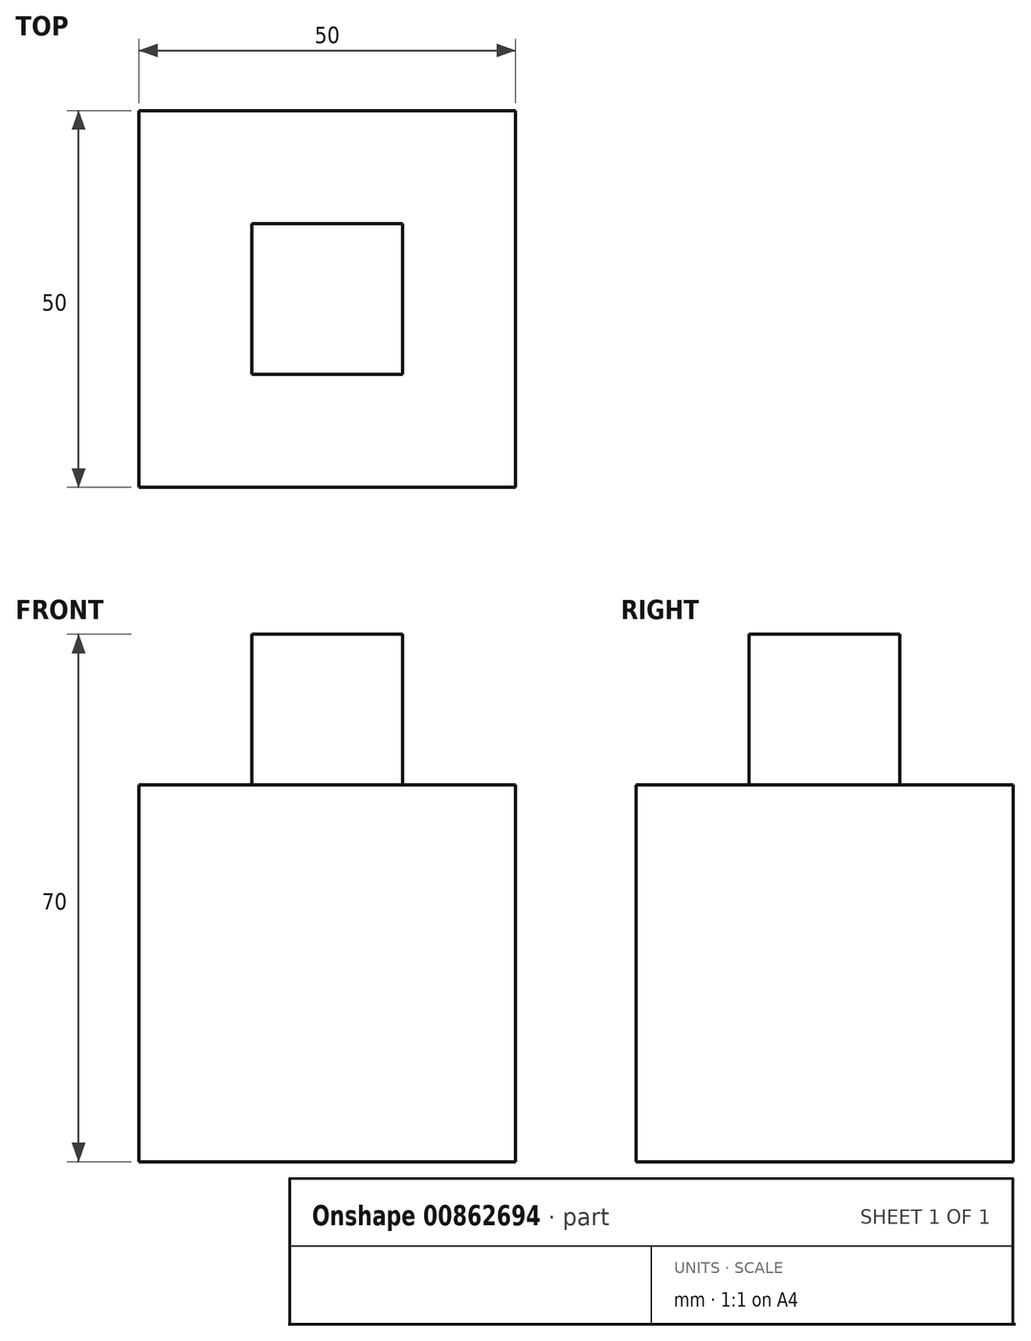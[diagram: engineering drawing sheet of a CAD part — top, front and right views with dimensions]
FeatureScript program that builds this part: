
annotation { "Feature Type Name" : "Feature", "Feature Type Description" : "" }
export const myFeature = defineFeature(function(context is Context, id is Id, definition is map)
    precondition{}
    {
        {
            var Q0;
            Q0=qCreatedBy(makeId("Front.planeOp"),FACE);
            var sketch = newSketch(context, id + "F0", { "sketchPlane" : qUnion([Q0])});
            skLineSegment(sketch, "E0.bottom", {"start": v(-25, -25) * mm, "end": v(25, -25) * mm});
            skLineSegment(sketch, "E0.top", {"start": v(-25, 25) * mm, "end": v(25, 25) * mm});
            skLineSegment(sketch, "E0.left", {"start": v(-25, -25) * mm, "end": v(-25, 25) * mm});
            skLineSegment(sketch, "E0.right", {"start": v(25, -25) * mm, "end": v(25, 25) * mm});
            skPoint(sketch, "E0.middle", {"position": v(0, 0) * mm});
            skLineSegment(sketch, "E1.bottom", {"start": v(10, 45) * mm, "end": v(-10, 45) * mm});
            skLineSegment(sketch, "E1.top", {"start": v(10, 25) * mm, "end": v(-10, 25) * mm});
            skLineSegment(sketch, "E1.left", {"start": v(10, 45) * mm, "end": v(10, 25) * mm});
            skLineSegment(sketch, "E1.right", {"start": v(-10, 45) * mm, "end": v(-10, 25) * mm});
            skPoint(sketch, "E1.middle", {"position": v(0, 35) * mm});
            skSolve(sketch);
        }
        {
            var Q0;
            Q0=makeQuery(id+"F0.imprint","IMPRINT",FACE,{"disambiguationData":[TD([[makeQuery(id+"F0.imprint","IMPRINT",EDGE,{"derivedFrom":sQuery(id+"F0.wireOp",EDGE,"E0.bottom")}),1.0]])]});
            extrude(context, id + "F1", {"entities" : qUnion([Q0]), "endBound" : BoundingType.SYMMETRIC, "depth" : 50 * mm, "offsetDistance" : 25 * mm});
        }
        {
            var Q0;
            Q0=makeQuery(id+"F0.imprint","IMPRINT",FACE,{"disambiguationData":[TD([[makeQuery(id+"F0.imprint","IMPRINT",EDGE,{"derivedFrom":sQuery(id+"F0.wireOp",EDGE,"E1.bottom")}),1.0]])]});
            extrude(context, id + "F2", {"entities" : qUnion([Q0]), "operationType" : NewBodyOperationType.ADD, "endBound" : BoundingType.SYMMETRIC, "depth" : 20 * mm, "offsetDistance" : 25 * mm});
        }
    });
